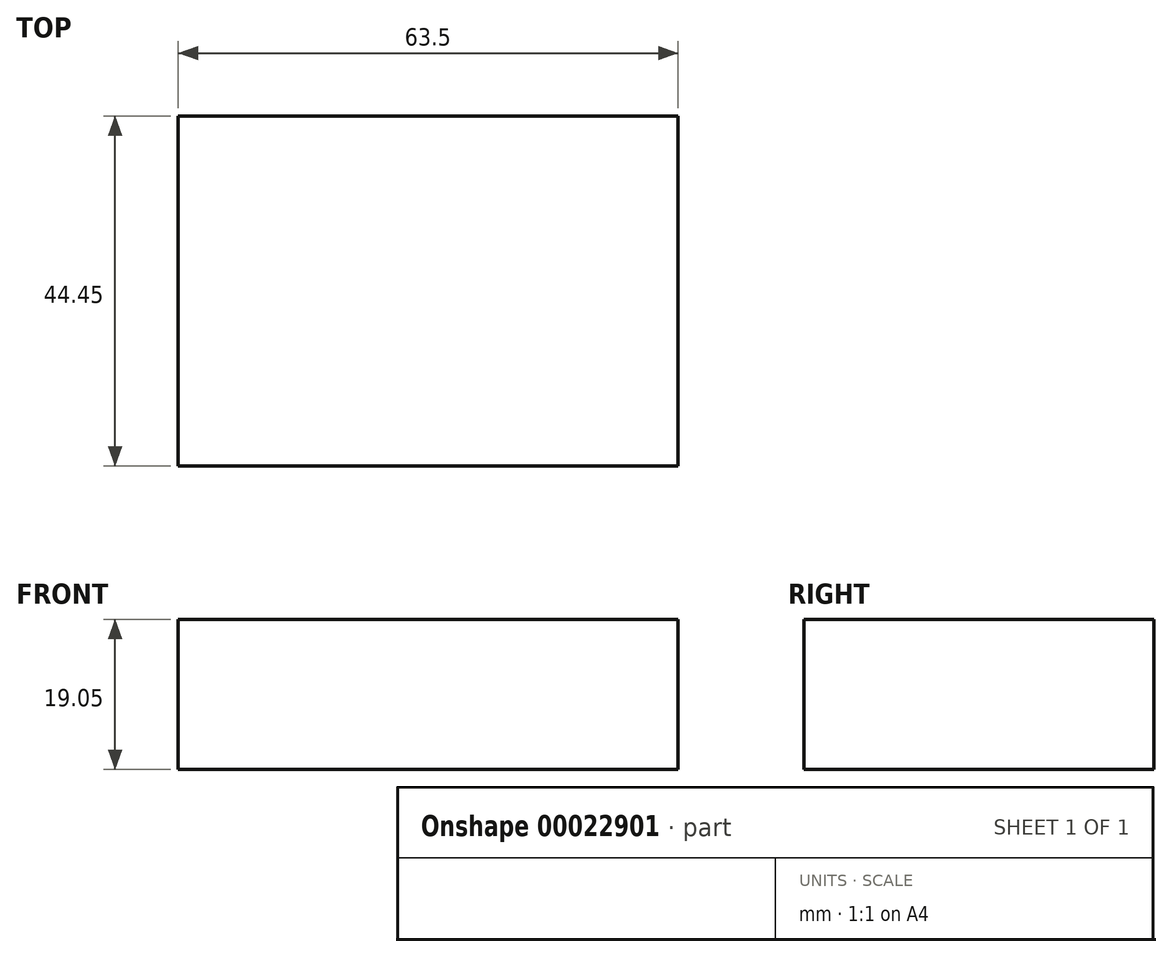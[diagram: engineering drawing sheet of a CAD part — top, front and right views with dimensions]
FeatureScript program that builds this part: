
annotation { "Feature Type Name" : "Feature", "Feature Type Description" : "" }
export const myFeature = defineFeature(function(context is Context, id is Id, definition is map)
    precondition{}
    {
        {
            var Q0;
            Q0=qCreatedBy(makeId("Top.planeOp"),FACE);
            var sketch = newSketch(context, id + "F0", { "sketchPlane" : qUnion([Q0])});
            skLineSegment(sketch, "E0.bottom", {"start": v(-149.8, 24.95) * mm, "end": v(-86.3, 24.95) * mm});
            skLineSegment(sketch, "E0.top", {"start": v(-149.8, -19.5) * mm, "end": v(-86.3, -19.5) * mm});
            skLineSegment(sketch, "E0.left", {"start": v(-149.8, 24.95) * mm, "end": v(-149.8, -19.5) * mm});
            skLineSegment(sketch, "E0.right", {"start": v(-86.3, 24.95) * mm, "end": v(-86.3, -19.5) * mm});
            skSolve(sketch);
        }
        {
            var Q0;
            Q0 = qSketchRegion(id + "F0", true);
            extrude(context, id + "F1", {"entities" : qUnion([Q0]), "depth" : 19.05 * mm});
        }
    });
